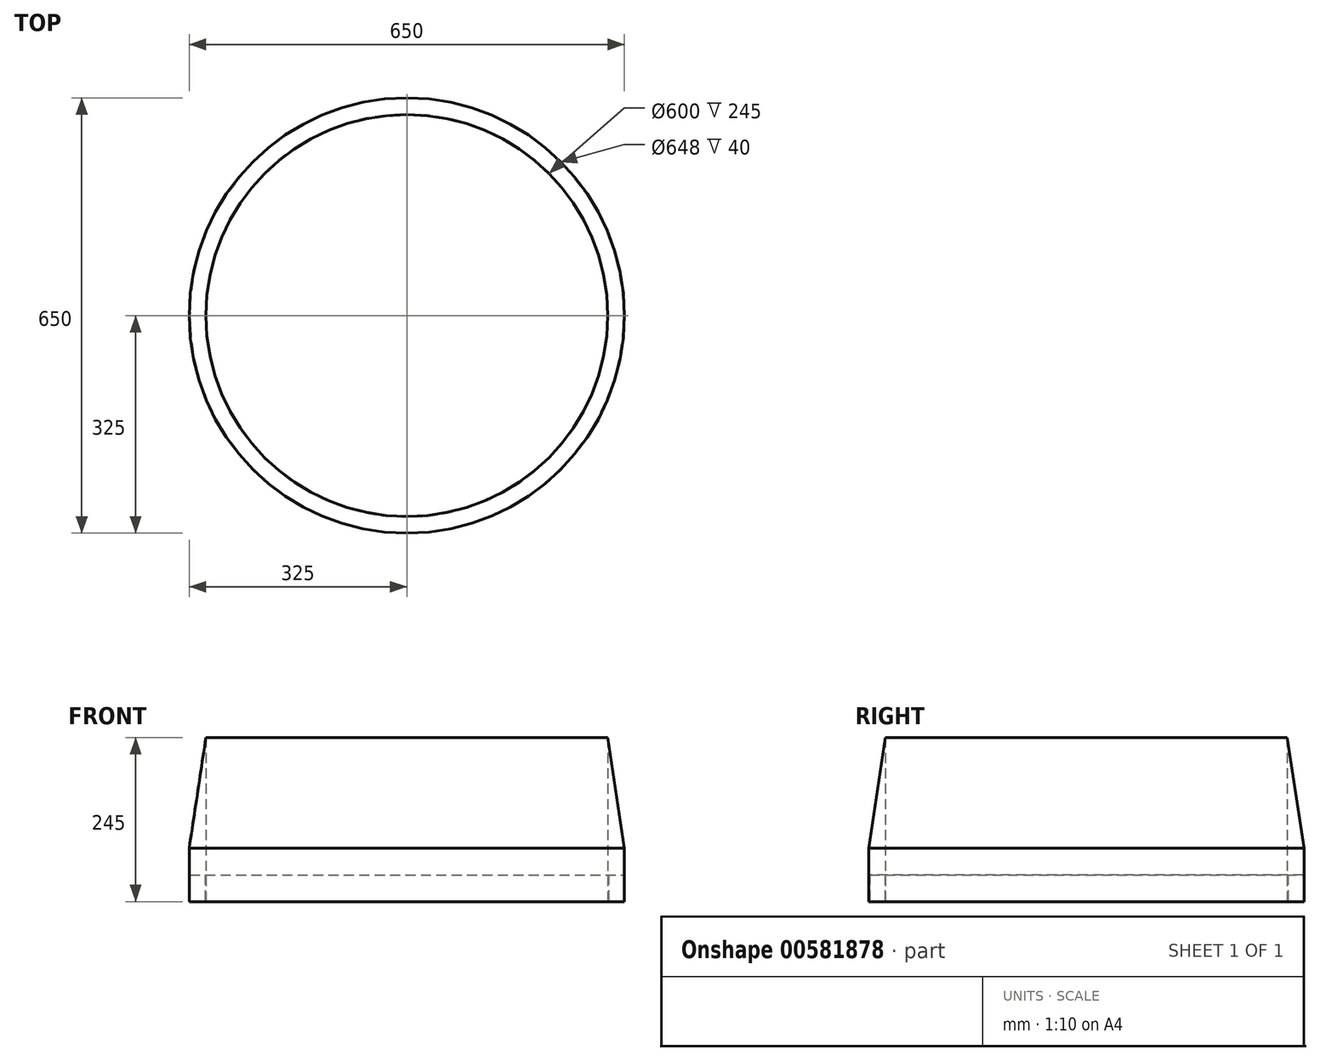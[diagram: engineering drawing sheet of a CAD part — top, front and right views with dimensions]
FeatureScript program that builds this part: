
annotation { "Feature Type Name" : "Feature", "Feature Type Description" : "" }
export const myFeature = defineFeature(function(context is Context, id is Id, definition is map)
    precondition{}
    {
        {
            var Q0;
            Q0=qCreatedBy(makeId("Front.planeOp"),FACE);
            var sketch = newSketch(context, id + "F0", { "sketchPlane" : qUnion([Q0])});
            skLineSegment(sketch, "E0", {"start": v(0, -139.25) * mm, "end": v(0, 240.83) * mm, "construction": true});
            skLineSegment(sketch, "E1", {"start": v(-300, -67.22) * mm, "end": v(-300, 177.78) * mm});
            skLineSegment(sketch, "E2", {"start": v(-300, 177.78) * mm, "end": v(-325, 12.78) * mm});
            skLineSegment(sketch, "E3", {"start": v(-325, 12.78) * mm, "end": v(-325, -67.22) * mm});
            skLineSegment(sketch, "E4", {"start": v(-325, -67.22) * mm, "end": v(-324, -67.22) * mm});
            skLineSegment(sketch, "E5", {"start": v(-324, -67.22) * mm, "end": v(-324, -27.22) * mm});
            skLineSegment(sketch, "E6", {"start": v(-324, -27.22) * mm, "end": v(-301, -27.22) * mm});
            skLineSegment(sketch, "E7", {"start": v(-301, -27.22) * mm, "end": v(-301, -67.22) * mm});
            skLineSegment(sketch, "E8", {"start": v(-301, -67.22) * mm, "end": v(-300, -67.22) * mm});
            skSolve(sketch);
        }
        {
            var Q0;
            Q0=qSketchRegion(id+"F0",true);
            var Q1;
            Q1=sQuery(id+"F0.wireOp",EDGE,"E0");
            revolve(context, id + "F1", {"entities" : qUnion([Q0]), "axis" : qUnion([Q1]), "revolveType" : RevolveType.FULL});
        }
    });
